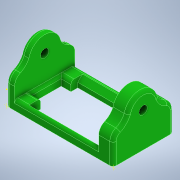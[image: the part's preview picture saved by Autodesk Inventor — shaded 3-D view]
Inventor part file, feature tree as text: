
AUTODESK INVENTOR PART (.ipt)
format: ipt  version: 2022 (Build 260153000, 153)  size: 240,128 bytes
history: native  units: in
note: dims shown in document units (in); Inventor stores cm internally (conversion verified against a paired STEP export)
features: sketch x5, extrude x3, fillet x2, chamfer x1
ambient origin geometry x8: Origin, YZ Plane, XZ Plane, XY Plane, X Axis, Y Axis, Z Axis, Center Point
bodies: Solid1 (feature_tree)
feature tree (11):
  extrude  "Extrusion1"  Depth=2.6378in TaperAngle=0.0deg
  extrude  "Extrusion2"  Depth=2.6378in TaperAngle=0.0deg
  sketch  "Sketch3"  dims[d12=0.1181in d13=0.0787in d14=45.0deg d15=0.0787in]
  fillet  "Fillet1"  Radius=0.0787in
  extrude  "Extrusion3"  Depth=0.1969in
  chamfer  "Chamfer1"  [1 undecoded]
  fillet  "Fillet2"  [1 undecoded]
  sketch  "Sketch5"
  sketch  "Sketch1"  dims[d5=2.6378in d6=0.0in d7=2.6378in d8=0.0in]
  sketch  "Sketch2"  dims[d9=0.2362in d10=2.6378in d11=0.0in]
  sketch  "Sketch4"  dims[d17=2.0866in d18=0.1969in]
note: 2 required parameter values undecoded (feature->parameter linkage not recoverable at this tier; creation-order binding heuristic only, values carry confidence <= 0.55)
